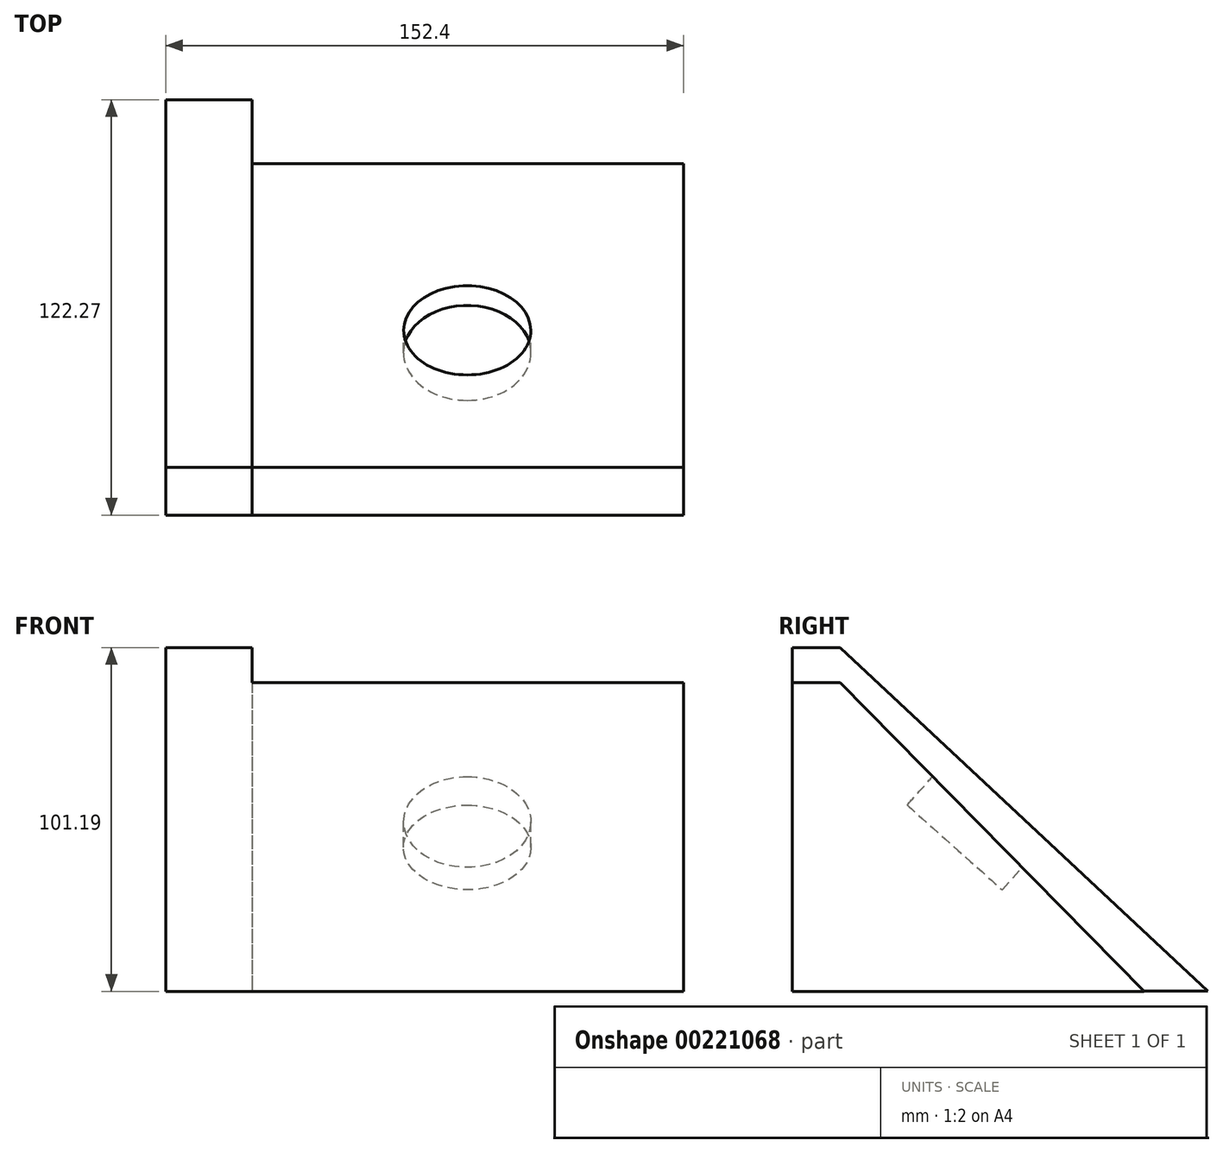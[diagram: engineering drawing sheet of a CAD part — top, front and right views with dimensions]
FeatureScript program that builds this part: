
annotation { "Feature Type Name" : "Feature", "Feature Type Description" : "" }
export const myFeature = defineFeature(function(context is Context, id is Id, definition is map)
    precondition{}
    {
        {
            var Q0;
            Q0=qCreatedBy(makeId("Right.planeOp"),FACE);
            var sketch = newSketch(context, id + "F0", { "sketchPlane" : qUnion([Q0])});
            skLineSegment(sketch, "E0.bottom", {"start": v(-49.06, 47.05) * mm, "end": v(54.43, 47.05) * mm});
            skLineSegment(sketch, "E0.top", {"start": v(-49.06, -43.79) * mm, "end": v(54.43, -43.79) * mm});
            skLineSegment(sketch, "E0.left", {"start": v(-49.06, 47.05) * mm, "end": v(-49.06, -43.79) * mm});
            skLineSegment(sketch, "E0.right", {"start": v(54.43, 47.05) * mm, "end": v(54.43, -43.79) * mm});
            skSolve(sketch);
        }
        {
            var Q0;
            Q0 = qSketchRegion(id + "F0", true);
            extrude(context, id + "F1", {"entities" : qUnion([Q0]), "depth" : 127 * mm});
        }
        {
            var Q0;
            Q0=makeQuery(id+"F1.opExtrude","CAP_FACE",FACE,{"disambiguationData":[OSD([sQuery(id+"F0.wireOp",EDGE,"E0.bottom"),sQuery(id+"F0.wireOp",EDGE,"E0.top"),sQuery(id+"F0.wireOp",EDGE,"E0.left"),sQuery(id+"F0.wireOp",EDGE,"E0.right")])],"isStart":false});
            var sketch = newSketch(context, id + "F2", { "sketchPlane" : qUnion([Q0])});
            skLineSegment(sketch, "E1", {"start": v(-45.23, 71.77) * mm, "end": v(64.2, -25.78) * mm});
            skLineSegment(sketch, "E2", {"start": v(64.2, -25.78) * mm, "end": v(62.47, 57.4) * mm});
            skLineSegment(sketch, "E3", {"start": v(62.47, 57.4) * mm, "end": v(-45.23, 71.77) * mm});
            skSolve(sketch);
        }
        {
            var Q0;
            Q0 = qSketchRegion(id + "F2", true);
            extrude(context, id + "F3", {"entities" : qUnion([Q0]), "operationType" : NewBodyOperationType.REMOVE, "endBound" : BoundingType.THROUGH_ALL, "oppositeDirection" : true, "depth" : 25.4 * mm});
        }
        {
            var Q0;
            Q0=makeQuery(id+"F3.boolean.opBoolean","COPY",FACE,{"derivedFrom":makeQuery(id+"F3.opExtrude","SWEPT_FACE",FACE,{"disambiguationData":[OSD([sQuery(id+"F2.wireOp",EDGE,"E1")])]})});
            var sketch = newSketch(context, id + "F4", { "sketchPlane" : qUnion([Q0])});
            skCircle(sketch, "E4", {"center": v(63.31, 0) * mm, "radius": 18.75 * mm});
            skSolve(sketch);
        }
        {
            var Q0;
            Q0=makeQuery(id+"F4.imprint","IMPRINT",FACE,{"disambiguationData":[TD([[makeQuery(id+"F4.imprint","IMPRINT",EDGE,{"derivedFrom":sQuery(id+"F4.wireOp",EDGE,"E4")}),1.0]])]});
            extrude(context, id + "F5", {"entities" : qUnion([Q0]), "operationType" : NewBodyOperationType.REMOVE, "oppositeDirection" : true, "depth" : 25.4 * mm});
        }
        {
            var Q0;
            Q0=makeQuery(id+"F1.opExtrude","CAP_FACE",FACE,{"disambiguationData":[OSD([sQuery(id+"F0.wireOp",EDGE,"E0.bottom"),sQuery(id+"F0.wireOp",EDGE,"E0.top"),sQuery(id+"F0.wireOp",EDGE,"E0.left"),sQuery(id+"F0.wireOp",EDGE,"E0.right")])],"isStart":true});
            var sketch = newSketch(context, id + "F6", { "sketchPlane" : qUnion([Q0])});
            skLineSegment(sketch, "E5", {"start": v(43.7, 55.86) * mm, "end": v(-58.83, -48.2) * mm});
            skLineSegment(sketch, "E6", {"start": v(-58.83, -48.2) * mm, "end": v(-54.43, 13.51) * mm});
            skLineSegment(sketch, "E7", {"start": v(-54.43, 13.51) * mm, "end": v(45.8, 72.54) * mm});
            skLineSegment(sketch, "E8", {"start": v(45.8, 72.54) * mm, "end": v(43.7, 55.86) * mm});
            skSolve(sketch);
        }
        {
            var Q0;
            Q0 = qSketchRegion(id + "F6", true);
            extrude(context, id + "F7", {"entities" : qUnion([Q0]), "operationType" : NewBodyOperationType.REMOVE, "endBound" : BoundingType.THROUGH_ALL, "oppositeDirection" : true, "depth" : 25.4 * mm});
        }
        {
            var Q0;
            Q0=makeQuery(id+"F1.opExtrude","CAP_FACE",FACE,{"disambiguationData":[OSD([sQuery(id+"F0.wireOp",EDGE,"E0.bottom"),sQuery(id+"F0.wireOp",EDGE,"E0.top"),sQuery(id+"F0.wireOp",EDGE,"E0.left"),sQuery(id+"F0.wireOp",EDGE,"E0.right")])],"isStart":true});
            var sketch = newSketch(context, id + "F8", { "sketchPlane" : qUnion([Q0])});
            skLineSegment(sketch, "E9", {"start": v(49.06, 47.05) * mm, "end": v(49.06, 57.4) * mm});
            skLineSegment(sketch, "E10", {"start": v(35, 47.05) * mm, "end": v(35, 57.4) * mm});
            skLineSegment(sketch, "E11", {"start": v(35, 57.4) * mm, "end": v(-73.2, -43.72) * mm});
            skLineSegment(sketch, "E12", {"start": v(-73.2, -43.72) * mm, "end": v(49.06, -43.79) * mm});
            skLineSegment(sketch, "E13", {"start": v(49.06, -43.79) * mm, "end": v(49.06, 57.4) * mm});
            skLineSegment(sketch, "E14", {"start": v(49.06, 57.4) * mm, "end": v(35, 57.4) * mm});
            skSolve(sketch);
        }
        {
            var Q0;
            Q0 = qSketchRegion(id + "F8", true);
            extrude(context, id + "F9", {"entities" : qUnion([Q0]), "operationType" : NewBodyOperationType.ADD, "depth" : 25.4 * mm});
        }
    });
